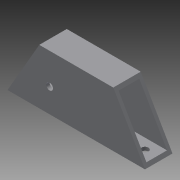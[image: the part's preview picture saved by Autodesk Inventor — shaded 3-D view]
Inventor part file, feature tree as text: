
AUTODESK INVENTOR PART (.ipt)
format: ipt  version: 2013 (Build 170138000, 138)  size: 112,640 bytes
history: native  units: in
note: dims shown in document units (in); Inventor stores cm internally (conversion verified against a paired STEP export)
features: extrude x5, sketch x5
ambient origin geometry x8: Origin, YZ Plane, XZ Plane, XY Plane, X Axis, Y Axis, Z Axis, Center Point
bodies: Solid1 (feature_tree)
feature tree (10):
  extrude  "Extrusion1"  Depth=2.0in
  extrude  "Extrusion2"  Depth=0.75in
  extrude  "Extrusion3"  Depth=99.0in TaperAngle=0.0deg
  extrude  "Extrusion4"  TaperAngle=120.0deg  [1 undecoded]
  extrude  "Extrusion5"  Depth=0.25in
  sketch  "Sketch1"  dims[d0=5.0in d1=2.0in]
  sketch  "Sketch2"  dims[d2=1.0in d3=0.0in d4=0.75in]
  sketch  "Sketch3"  dims[d5=1.75in d6=99.0in d7=0.0in]
  sketch  "Sketch4"  dims[d8=60.0deg d9=120.0deg]
  sketch  "Sketch5"  dims[d10=99.0in d11=0.0in d12=0.25in d13=0.25in d14=99.0in d15=0.0in d16=0.375in d17=0.8755in d18=90.0deg d19=0.5in d20=0.25in d21=99.0in d22=0.0in]
note: 1 required parameter value undecoded (feature->parameter linkage not recoverable at this tier; creation-order binding heuristic only, values carry confidence <= 0.55)
